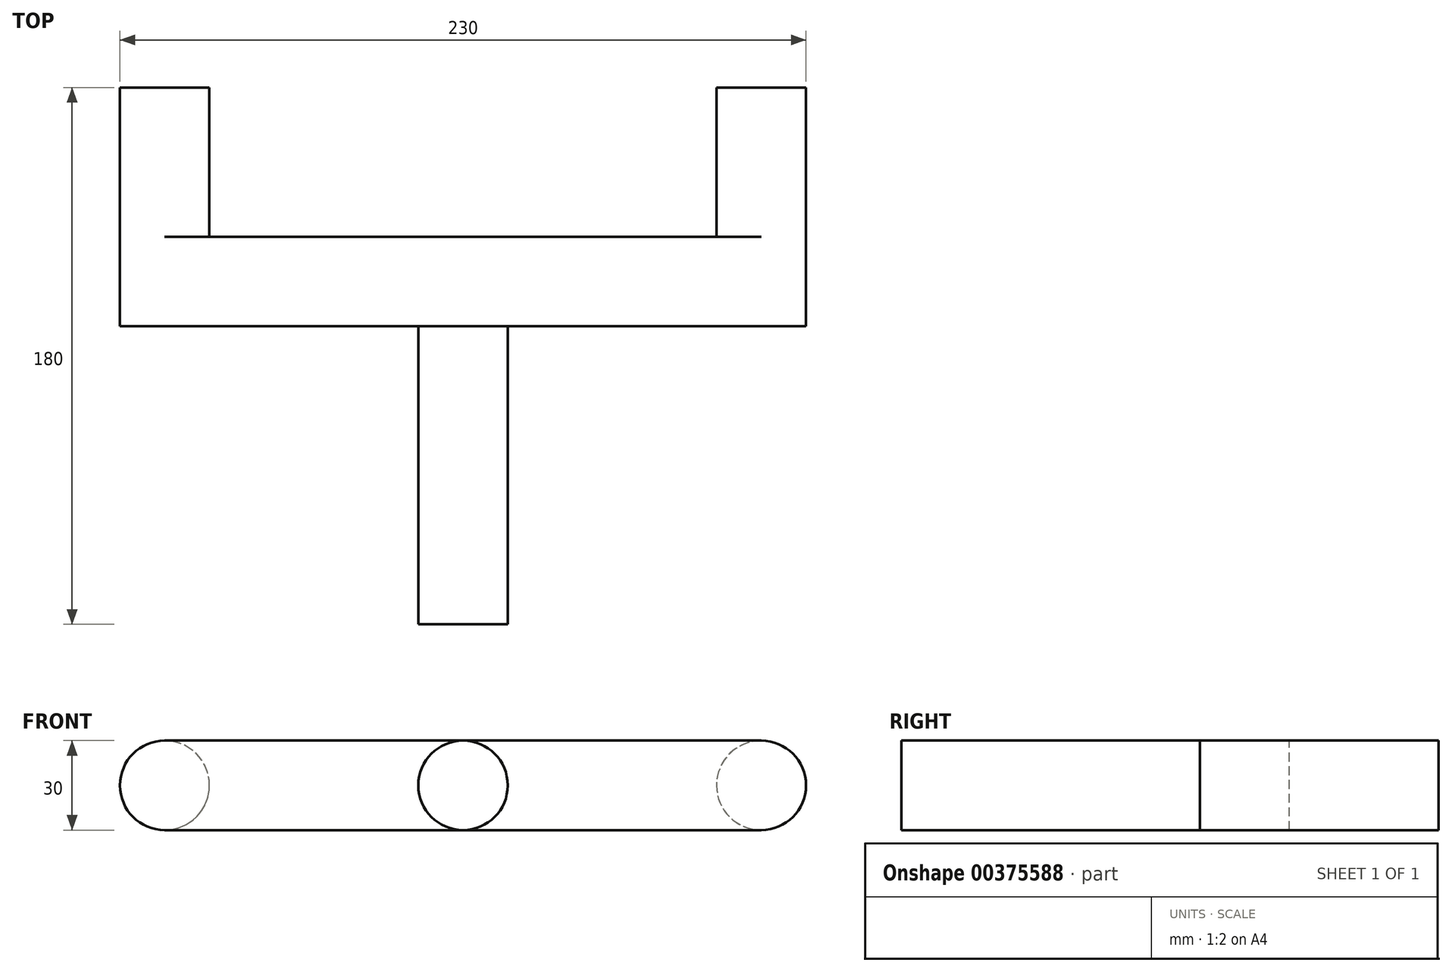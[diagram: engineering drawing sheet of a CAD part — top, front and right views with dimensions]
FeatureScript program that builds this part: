
annotation { "Feature Type Name" : "Feature", "Feature Type Description" : "" }
export const myFeature = defineFeature(function(context is Context, id is Id, definition is map)
    precondition{}
    {
        {
            var Q0;
            Q0=qCreatedBy(makeId("Front.planeOp"),FACE);
            var sketch = newSketch(context, id + "F0", { "sketchPlane" : qUnion([Q0])});
            skArc(sketch, "E0", {"start": v(-100, 15) * mm, "mid": v(-115, 0) * mm, "end": v(-100, -15) * mm});
            skArc(sketch, "E1", {"start": v(100, -15) * mm, "mid": v(115, 0) * mm, "end": v(100, 15) * mm});
            skLineSegment(sketch, "E2", {"start": v(-100, 15) * mm, "end": v(100, 15) * mm});
            skLineSegment(sketch, "E3", {"start": v(-100, -15) * mm, "end": v(100, -15) * mm});
            skSolve(sketch);
        }
        {
            var Q0;
            Q0=makeQuery(id+"F0.imprint","IMPRINT",FACE,{"disambiguationData":[TD([[makeQuery(id+"F0.imprint","IMPRINT",EDGE,{"derivedFrom":sQuery(id+"F0.wireOp",EDGE,"E0")}),1.0]])]});
            extrude(context, id + "F1", {"entities" : qUnion([Q0]), "depth" : 30 * mm});
        }
        {
            var Q0;
            Q0=makeQuery(id+"F1.opExtrude","CAP_FACE",FACE,{"disambiguationData":[OSD([sQuery(id+"F0.wireOp",EDGE,"E0"),sQuery(id+"F0.wireOp",EDGE,"E1"),sQuery(id+"F0.wireOp",EDGE,"E2"),sQuery(id+"F0.wireOp",EDGE,"E3")])],"isStart":false});
            var sketch = newSketch(context, id + "F2", { "sketchPlane" : qUnion([Q0])});
            skCircle(sketch, "E4", {"center": v(0, 0) * mm, "radius": 15 * mm});
            skSolve(sketch);
        }
        {
            var Q0;
            {var subQ0=sQuery(id+"F2.wireOp",EDGE,"E4");var subQ1=makeQuery(id+"F2.imprint","INTERSECT",VERTEX,{"derivedFrom":[makeQuery(id+"F1.opExtrude","CAP_EDGE",EDGE,{"disambiguationData":[OSD([sQuery(id+"F0.wireOp",EDGE,"E2")])],"isStart":false}),subQ0]});Q0=makeQuery(id+"F2.imprint","IMPRINT",FACE,{"disambiguationData":[TD([[makeQuery(id+"F2.imprint","IMPRINT",EDGE,{"disambiguationData":[TD([[subQ1,-1.0]])],"derivedFrom":subQ0}),1.0]])]});}
            extrude(context, id + "F3", {"entities" : qUnion([Q0]), "operationType" : NewBodyOperationType.ADD, "depth" : 100 * mm});
        }
        {
            var Q0;
            Q0=makeQuery(id+"F1.opExtrude","CAP_FACE",FACE,{"disambiguationData":[OSD([sQuery(id+"F0.wireOp",EDGE,"E0"),sQuery(id+"F0.wireOp",EDGE,"E1"),sQuery(id+"F0.wireOp",EDGE,"E2"),sQuery(id+"F0.wireOp",EDGE,"E3")])],"isStart":true});
            var sketch = newSketch(context, id + "F4", { "sketchPlane" : qUnion([Q0])});
            skLineSegment(sketch, "E5", {"start": v(0, 0) * mm, "end": v(-100, 0) * mm});
            skLineSegment(sketch, "E6", {"start": v(0, 0) * mm, "end": v(100, 0) * mm});
            skCircle(sketch, "E7", {"center": v(-100, 0) * mm, "radius": 15 * mm});
            skCircle(sketch, "E8", {"center": v(100, 0) * mm, "radius": 15 * mm});
            skSolve(sketch);
        }
        {
            var Q0;
            {var subQ0=sQuery(id+"F4.wireOp",EDGE,"E7");var subQ1=makeQuery(id+"F4.imprint","INTERSECT",VERTEX,{"derivedFrom":[makeQuery(id+"F1.opExtrude","CAP_EDGE",EDGE,{"disambiguationData":[OSD([sQuery(id+"F0.wireOp",EDGE,"E2")])],"isStart":true}),subQ0]});var subQ2=makeQuery(id+"F4.imprint","INTERSECT",VERTEX,{"derivedFrom":[sQuery(id+"F4.wireOp",EDGE,"E5"),subQ0]});Q0=makeQuery(id+"F4.imprint","IMPRINT",FACE,{"disambiguationData":[TD([[makeQuery(id+"F4.imprint","IMPRINT",EDGE,{"disambiguationData":[TD([[subQ1,1.0],[subQ2,-1.0]])],"derivedFrom":subQ0}),1.0]])]});}
            var Q1;
            {var subQ0=sQuery(id+"F4.wireOp",EDGE,"E8");var subQ1=makeQuery(id+"F4.imprint","INTERSECT",VERTEX,{"derivedFrom":[makeQuery(id+"F1.opExtrude","CAP_EDGE",EDGE,{"disambiguationData":[OSD([sQuery(id+"F0.wireOp",EDGE,"E2")])],"isStart":true}),subQ0]});var subQ2=makeQuery(id+"F4.imprint","INTERSECT",VERTEX,{"derivedFrom":[makeQuery(id+"F1.opExtrude","CAP_EDGE",EDGE,{"disambiguationData":[OSD([sQuery(id+"F0.wireOp",EDGE,"E3")])],"isStart":true}),subQ0]});Q1=makeQuery(id+"F4.imprint","IMPRINT",FACE,{"disambiguationData":[TD([[makeQuery(id+"F4.imprint","IMPRINT",EDGE,{"disambiguationData":[TD([[subQ1,-1.0],[subQ2,1.0]])],"derivedFrom":subQ0}),-1.0]])]});}
            extrude(context, id + "F5", {"entities" : qUnion([Q0, Q1]), "operationType" : NewBodyOperationType.ADD, "depth" : 50 * mm});
        }
    });
